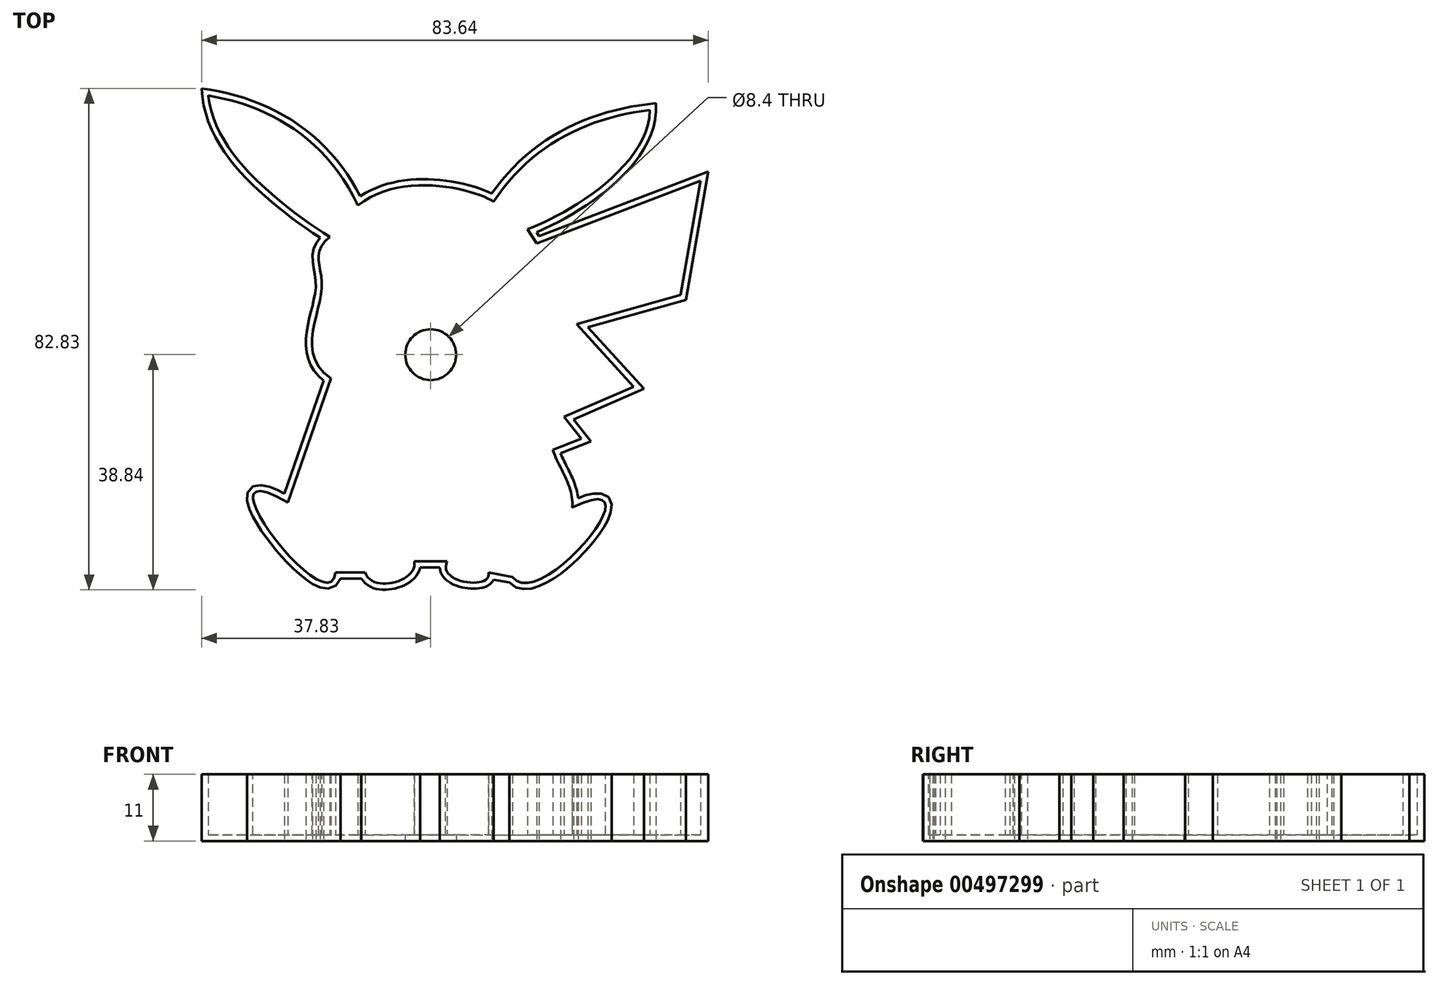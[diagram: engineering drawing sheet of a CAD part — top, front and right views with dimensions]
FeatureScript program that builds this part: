
annotation { "Feature Type Name" : "Feature", "Feature Type Description" : "" }
export const myFeature = defineFeature(function(context is Context, id is Id, definition is map)
    precondition{}
    {
        {
            var Q0;
            Q0=qCreatedBy(makeId("Top.planeOp"),FACE);
            var sketch = newSketch(context, id + "F0", { "sketchPlane" : qUnion([Q0])});
            skFitSpline(sketch, "E0", {"points": [v(10.38, 25.3) * mm, v(-12.03, 24.66) * mm], "startDerivative": vector(-9.01, 5.76) * mm, "endDerivative": vector(-22.56, -17.74) * mm});
            skFitSpline(sketch, "E1", {"points": [v(-12.03, 24.66) * mm, v(-36.7, 42.8) * mm], "startDerivative": vector(-16.64, 35.7) * mm, "endDerivative": vector(-26.64, 4.3) * mm});
            skFitSpline(sketch, "E2", {"points": [v(-36.7, 42.8) * mm, v(-16.67, 19.47) * mm], "startDerivative": vector(2.96, -29.35) * mm, "endDerivative": vector(24.8, -16.1) * mm});
            skFitSpline(sketch, "E3", {"points": [v(-16.67, 19.47) * mm, v(-17.97, 11.3) * mm, v(-16.5, -3.9) * mm], "startDerivative": vector(-23.28, -18.63) * mm, "endDerivative": vector(30.7, -20.33) * mm});
            skFitSpline(sketch, "E4", {"points": [v(-16.5, -3.9) * mm, v(-23.6, -24.43) * mm], "startDerivative": vector(-7.1, -20.53) * mm, "endDerivative": vector(-7.1, -20.53) * mm});
            skFitSpline(sketch, "E5", {"points": [v(-23.6, -24.43) * mm, v(-15.72, -35.98) * mm], "startDerivative": vector(-48.72, 28.75) * mm, "endDerivative": vector(2.75, 26.93) * mm});
            skFitSpline(sketch, "E6", {"points": [v(-15.72, -35.98) * mm, v(-10.8, -35.98) * mm], "startDerivative": vector(4.9, 0) * mm, "endDerivative": vector(4.9, 0) * mm});
            skFitSpline(sketch, "E7", {"points": [v(-10.8, -35.98) * mm, v(-2.72, -34.14) * mm], "startDerivative": vector(3.24, -10.65) * mm, "endDerivative": vector(-2.1, 10) * mm});
            skFitSpline(sketch, "E8", {"points": [v(-2.72, -34.14) * mm, v(2.73, -34.14) * mm], "startDerivative": vector(5.45, 0) * mm, "endDerivative": vector(5.45, 0) * mm});
            skFitSpline(sketch, "E9", {"points": [v(2.73, -34.14) * mm, v(9.53, -35.98) * mm], "startDerivative": vector(-5.66, -10.81) * mm, "endDerivative": vector(-2.43, 9.03) * mm});
            skFitSpline(sketch, "E10", {"points": [v(9.53, -35.98) * mm, v(13.52, -36.73) * mm], "startDerivative": vector(4, -0.76) * mm, "endDerivative": vector(4, -0.76) * mm});
            skFitSpline(sketch, "E11", {"points": [v(13.52, -36.73) * mm, v(23.34, -25.24) * mm], "startDerivative": vector(13.76, -18.74) * mm, "endDerivative": vector(-45.64, -22.04) * mm});
            skFitSpline(sketch, "E12", {"points": [v(23.34, -25.24) * mm, v(20.16, -15.71) * mm], "startDerivative": vector(1.13, 10.24) * mm, "endDerivative": vector(-3.18, 9.53) * mm});
            skLineSegment(sketch, "E13", {"start": v(20.16, -15.71) * mm, "end": v(24.85, -13.88) * mm});
            skLineSegment(sketch, "E14", {"start": v(24.85, -13.88) * mm, "end": v(22.02, -10.29) * mm});
            skLineSegment(sketch, "E15", {"start": v(22.02, -10.29) * mm, "end": v(33.5, -5.28) * mm});
            skLineSegment(sketch, "E16", {"start": v(33.5, -5.28) * mm, "end": v(24.11, 5.03) * mm});
            skLineSegment(sketch, "E17", {"start": v(24.11, 5.03) * mm, "end": v(41.26, 9.84) * mm});
            skLineSegment(sketch, "E18", {"start": v(41.26, 9.84) * mm, "end": v(44.52, 28.7) * mm});
            skLineSegment(sketch, "E19", {"start": v(44.52, 28.7) * mm, "end": v(17.49, 18.37) * mm});
            skFitSpline(sketch, "E20", {"points": [v(10.38, 25.3) * mm, v(36.19, 40.4) * mm], "startDerivative": vector(18.15, 27.5) * mm, "endDerivative": vector(31.58, 3.66) * mm});
            skFitSpline(sketch, "E21", {"points": [v(36.19, 40.4) * mm, v(15.97, 20.73) * mm], "startDerivative": vector(-0.69, -28.84) * mm, "endDerivative": vector(-18.08, -6.64) * mm});
            skFitSpline(sketch, "E22", {"points": [v(15.97, 20.73) * mm, v(17.49, 18.37) * mm], "startDerivative": vector(1.52, -2.36) * mm, "endDerivative": vector(1.52, -2.36) * mm});
            skLineSegment(sketch, "E23", {"start": v(-36.7, 42.8) * mm, "end": v(23.5, -33.1) * mm, "construction": true});
            skSolve(sketch);
        }
        {
            var Q0;
            Q0=makeQuery(id+"F0.imprint","IMPRINT",FACE,{"disambiguationData":[TD([[makeQuery(id+"F0.imprint","IMPRINT",EDGE,{"derivedFrom":sQuery(id+"F0.wireOp",EDGE,"E0")}),1.0]])]});
            extrude(context, id + "F1", {"entities" : qUnion([Q0]), "depth" : 10 * mm});
        }
        {
            var Q0;
            Q0=makeQuery(id+"F1.opExtrude","CAP_FACE",FACE,{"disambiguationData":[OSD([sQuery(id+"F0.wireOp",EDGE,"E0"),sQuery(id+"F0.wireOp",EDGE,"E1"),sQuery(id+"F0.wireOp",EDGE,"E2"),sQuery(id+"F0.wireOp",EDGE,"E3"),sQuery(id+"F0.wireOp",EDGE,"E4"),sQuery(id+"F0.wireOp",EDGE,"E5"),sQuery(id+"F0.wireOp",EDGE,"E6"),sQuery(id+"F0.wireOp",EDGE,"E7"),sQuery(id+"F0.wireOp",EDGE,"E8"),sQuery(id+"F0.wireOp",EDGE,"E9"),sQuery(id+"F0.wireOp",EDGE,"E10"),sQuery(id+"F0.wireOp",EDGE,"E11"),sQuery(id+"F0.wireOp",EDGE,"E12"),sQuery(id+"F0.wireOp",EDGE,"E13"),sQuery(id+"F0.wireOp",EDGE,"E14"),sQuery(id+"F0.wireOp",EDGE,"E15"),sQuery(id+"F0.wireOp",EDGE,"E16"),sQuery(id+"F0.wireOp",EDGE,"E17"),sQuery(id+"F0.wireOp",EDGE,"E18"),sQuery(id+"F0.wireOp",EDGE,"E19"),sQuery(id+"F0.wireOp",EDGE,"E20"),sQuery(id+"F0.wireOp",EDGE,"E21"),sQuery(id+"F0.wireOp",EDGE,"E22")])],"isStart":false});
            shell(context, id + "F2", {"entities" : qUnion([Q0]), "thickness" : 1 * mm, "oppositeDirection" : true});
        }
        {
            var Q0;
            Q0=makeQuery(id+"F1.opExtrude","CAP_FACE",FACE,{"disambiguationData":[OSD([sQuery(id+"F0.wireOp",EDGE,"E0"),sQuery(id+"F0.wireOp",EDGE,"E1"),sQuery(id+"F0.wireOp",EDGE,"E2"),sQuery(id+"F0.wireOp",EDGE,"E3"),sQuery(id+"F0.wireOp",EDGE,"E4"),sQuery(id+"F0.wireOp",EDGE,"E5"),sQuery(id+"F0.wireOp",EDGE,"E6"),sQuery(id+"F0.wireOp",EDGE,"E7"),sQuery(id+"F0.wireOp",EDGE,"E8"),sQuery(id+"F0.wireOp",EDGE,"E9"),sQuery(id+"F0.wireOp",EDGE,"E10"),sQuery(id+"F0.wireOp",EDGE,"E11"),sQuery(id+"F0.wireOp",EDGE,"E12"),sQuery(id+"F0.wireOp",EDGE,"E13"),sQuery(id+"F0.wireOp",EDGE,"E14"),sQuery(id+"F0.wireOp",EDGE,"E15"),sQuery(id+"F0.wireOp",EDGE,"E16"),sQuery(id+"F0.wireOp",EDGE,"E17"),sQuery(id+"F0.wireOp",EDGE,"E18"),sQuery(id+"F0.wireOp",EDGE,"E19"),sQuery(id+"F0.wireOp",EDGE,"E20"),sQuery(id+"F0.wireOp",EDGE,"E21"),sQuery(id+"F0.wireOp",EDGE,"E22")])],"isStart":true});
            var sketch = newSketch(context, id + "F3", { "sketchPlane" : qUnion([Q0])});
            skCircle(sketch, "E24", {"center": v(0, 0) * mm, "radius": 4.2 * mm});
            skSolve(sketch);
        }
        {
            var Q0;
            Q0 = qSketchRegion(id + "F3", true);
            extrude(context, id + "F4", {"entities" : qUnion([Q0]), "operationType" : NewBodyOperationType.REMOVE, "oppositeDirection" : true, "depth" : 14.6 * mm});
        }
    });
